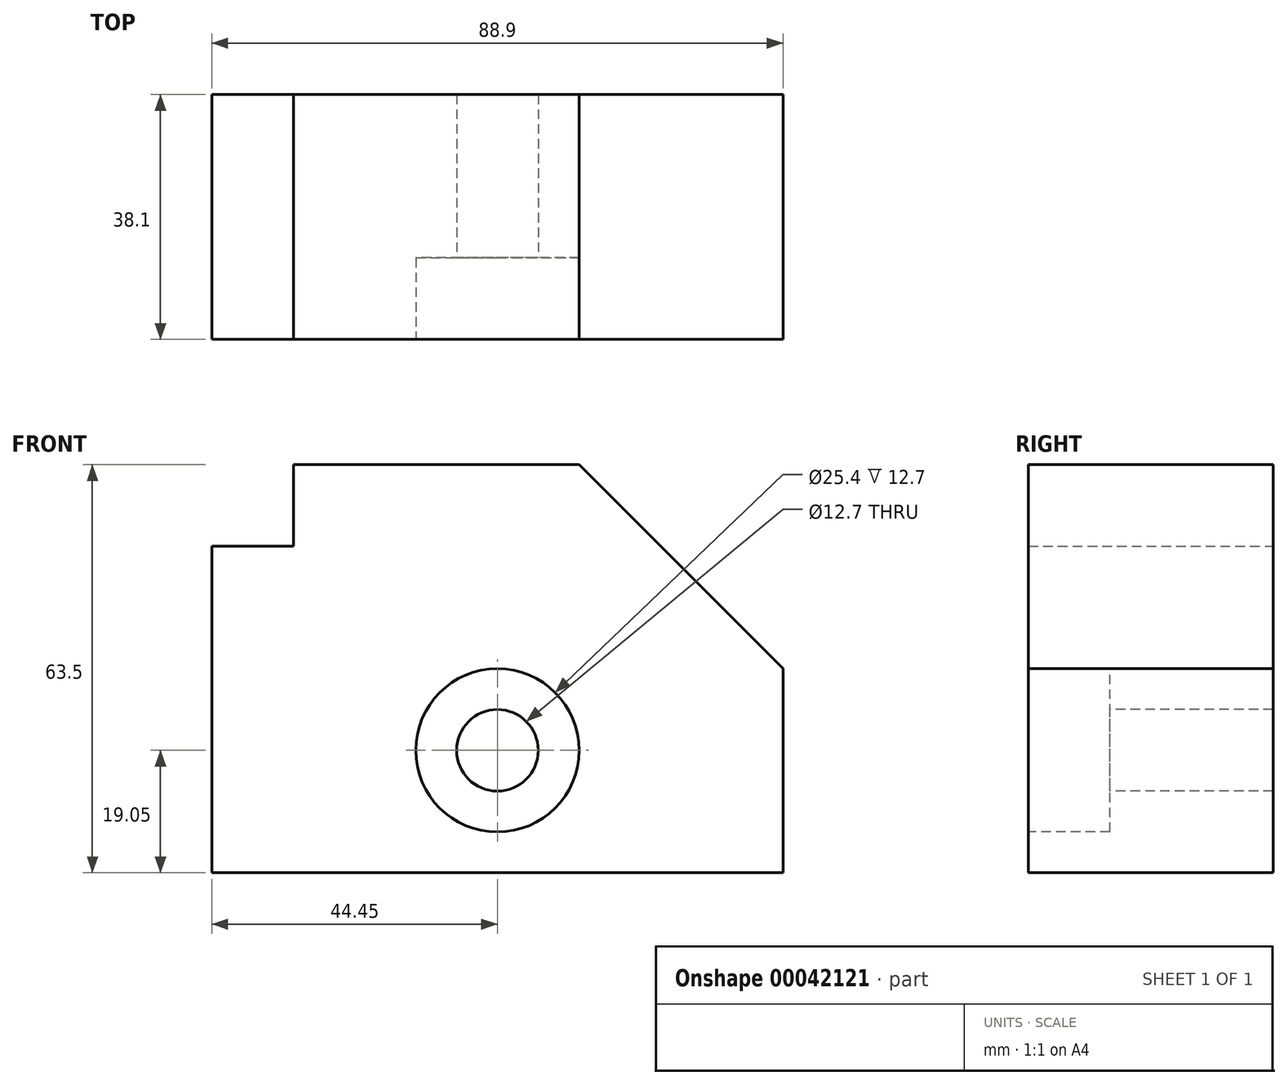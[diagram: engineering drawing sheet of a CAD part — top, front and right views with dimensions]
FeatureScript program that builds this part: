
annotation { "Feature Type Name" : "Feature", "Feature Type Description" : "" }
export const myFeature = defineFeature(function(context is Context, id is Id, definition is map)
    precondition{}
    {
        {
            var Q0;
            Q0=qCreatedBy(makeId("Front.planeOp"),FACE);
            var sketch = newSketch(context, id + "F0", { "sketchPlane" : qUnion([Q0])});
            skLineSegment(sketch, "E0.bottom", {"start": v(0, 0) * mm, "end": v(88.9, 0) * mm});
            skLineSegment(sketch, "E0.top", {"start": v(12.7, 63.5) * mm, "end": v(57.15, 63.5) * mm});
            skLineSegment(sketch, "E0.left", {"start": v(0, 0) * mm, "end": v(0, 50.8) * mm});
            skLineSegment(sketch, "E0.right", {"start": v(88.9, 0) * mm, "end": v(88.9, 31.75) * mm});
            skLineSegment(sketch, "E1", {"start": v(88.9, 31.75) * mm, "end": v(57.15, 63.5) * mm});
            skPoint(sketch, "E2.orphan", {"position": v(88.9, 63.5) * mm});
            skLineSegment(sketch, "E3", {"start": v(12.7, 63.5) * mm, "end": v(12.7, 50.8) * mm});
            skLineSegment(sketch, "E4", {"start": v(12.7, 50.8) * mm, "end": v(0, 50.8) * mm});
            skSolve(sketch);
        }
        {
            var Q0;
            Q0=makeQuery(id+"F0.imprint","IMPRINT",FACE,{"disambiguationData":[TD([[makeQuery(id+"F0.imprint","IMPRINT",EDGE,{"derivedFrom":sQuery(id+"F0.wireOp",EDGE,"E0.bottom")}),1.0]])]});
            extrude(context, id + "F1", {"entities" : qUnion([Q0]), "depth" : 38.1 * mm});
        }
        {
            var Q0;
            Q0=makeQuery(id+"F1.opExtrude","CAP_FACE",FACE,{"disambiguationData":[OSD([sQuery(id+"F0.wireOp",EDGE,"E0.bottom"),sQuery(id+"F0.wireOp",EDGE,"E0.top"),sQuery(id+"F0.wireOp",EDGE,"E0.left"),sQuery(id+"F0.wireOp",EDGE,"E0.right"),sQuery(id+"F0.wireOp",EDGE,"E1"),sQuery(id+"F0.wireOp",EDGE,"E3"),sQuery(id+"F0.wireOp",EDGE,"E4")])],"isStart":false});
            var sketch = newSketch(context, id + "F2", { "sketchPlane" : qUnion([Q0])});
            skCircle(sketch, "E5", {"center": v(44.45, 19.05) * mm, "radius": 12.7 * mm});
            skPoint(sketch, "E5.centerSnap0", {"position": v(44.45, 0) * mm});
            skSolve(sketch);
        }
        {
            var Q0;
            Q0 = qSketchRegion(id + "F2", true);
            extrude(context, id + "F3", {"entities" : qUnion([Q0]), "operationType" : NewBodyOperationType.REMOVE, "oppositeDirection" : true, "depth" : 12.7 * mm});
        }
        {
            var Q0;
            Q0=makeQuery(id+"F3.boolean.opBoolean","COPY",FACE,{"derivedFrom":makeQuery(id+"F3.opExtrude","CAP_FACE",FACE,{"disambiguationData":[OSD([sQuery(id+"F2.wireOp",EDGE,"E5")])],"isStart":false})});
            var sketch = newSketch(context, id + "F4", { "sketchPlane" : qUnion([Q0])});
            skCircle(sketch, "E6", {"center": v(44.45, 19.05) * mm, "radius": 6.35 * mm});
            skSolve(sketch);
        }
        {
            var Q0;
            Q0 = qSketchRegion(id + "F4", true);
            extrude(context, id + "F5", {"entities" : qUnion([Q0]), "operationType" : NewBodyOperationType.REMOVE, "endBound" : BoundingType.THROUGH_ALL, "oppositeDirection" : true, "depth" : 25.4 * mm});
        }
    });
